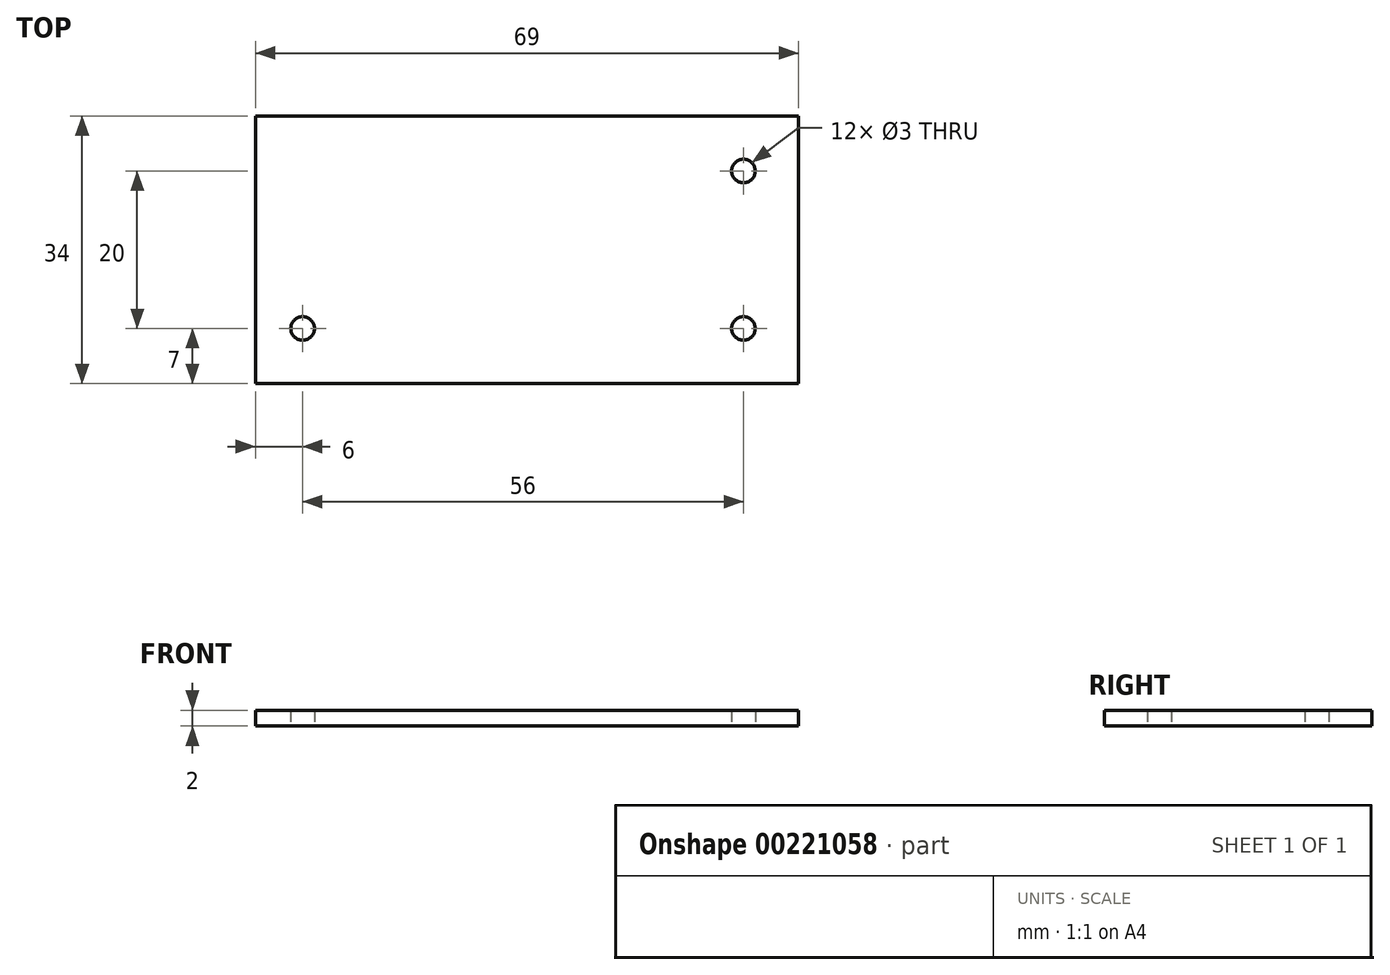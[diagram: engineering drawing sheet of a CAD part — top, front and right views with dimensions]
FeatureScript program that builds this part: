
annotation { "Feature Type Name" : "Feature", "Feature Type Description" : "" }
export const myFeature = defineFeature(function(context is Context, id is Id, definition is map)
    precondition{}
    {
        {
            var Q0;
            Q0=qCreatedBy(makeId("Top.planeOp"),FACE);
            var sketch = newSketch(context, id + "F0", { "sketchPlane" : qUnion([Q0])});
            skLineSegment(sketch, "E0.bottom", {"start": v(-32.5, 15) * mm, "end": v(32.5, 15) * mm});
            skLineSegment(sketch, "E0.top", {"start": v(-32.5, -15) * mm, "end": v(32.5, -15) * mm});
            skLineSegment(sketch, "E0.left", {"start": v(-32.5, 15) * mm, "end": v(-32.5, -15) * mm});
            skLineSegment(sketch, "E0.right", {"start": v(32.5, 15) * mm, "end": v(32.5, -15) * mm});
            skCircle(sketch, "E1", {"center": v(27.5, 10) * mm, "radius": 1.5 * mm});
            skCircle(sketch, "E2", {"center": v(27.5, -10) * mm, "radius": 1.5 * mm});
            skCircle(sketch, "E3", {"center": v(-28.5, -10) * mm, "radius": 1.5 * mm});
            skLineSegment(sketch, "E4", {"start": v(-32.5, 15) * mm, "end": v(-32.5, 17) * mm});
            skLineSegment(sketch, "E5", {"start": v(-32.5, 17) * mm, "end": v(32.5, 17) * mm});
            skLineSegment(sketch, "E6", {"start": v(32.5, 17) * mm, "end": v(32.5, 15) * mm});
            skLineSegment(sketch, "E7", {"start": v(-32.5, 17) * mm, "end": v(-34.5, 17) * mm});
            skLineSegment(sketch, "E8", {"start": v(-34.5, 17) * mm, "end": v(-34.5, -17) * mm});
            skLineSegment(sketch, "E9", {"start": v(-34.5, -17) * mm, "end": v(-32.5, -17) * mm});
            skLineSegment(sketch, "E10", {"start": v(-32.5, -17) * mm, "end": v(-32.5, -15) * mm});
            skLineSegment(sketch, "E11", {"start": v(-32.5, -17) * mm, "end": v(32.5, -17) * mm});
            skLineSegment(sketch, "E12", {"start": v(32.5, -17) * mm, "end": v(32.5, -15) * mm});
            skLineSegment(sketch, "E13", {"start": v(32.5, -17) * mm, "end": v(34.5, -17) * mm});
            skLineSegment(sketch, "E14", {"start": v(34.5, -17) * mm, "end": v(34.5, 17) * mm});
            skLineSegment(sketch, "E15", {"start": v(34.5, 17) * mm, "end": v(32.5, 17) * mm});
            skSolve(sketch);
        }
        {
            var Q0;
            Q0=makeQuery(id+"F0.imprint","IMPRINT",FACE,{"disambiguationData":[TD([[makeQuery(id+"F0.imprint","IMPRINT",EDGE,{"derivedFrom":sQuery(id+"F0.wireOp",EDGE,"E0.bottom")}),-1.0]])]});
            var Q1;
            Q1=makeQuery(id+"F0.imprint","IMPRINT",FACE,{"disambiguationData":[TD([[makeQuery(id+"F0.imprint","IMPRINT",EDGE,{"derivedFrom":sQuery(id+"F0.wireOp",EDGE,"E0.left")}),-1.0]])]});
            var Q2;
            Q2=makeQuery(id+"F0.imprint","IMPRINT",FACE,{"disambiguationData":[TD([[makeQuery(id+"F0.imprint","IMPRINT",EDGE,{"derivedFrom":sQuery(id+"F0.wireOp",EDGE,"E0.bottom")}),1.0]])]});
            var Q3;
            Q3=makeQuery(id+"F0.imprint","IMPRINT",FACE,{"disambiguationData":[TD([[makeQuery(id+"F0.imprint","IMPRINT",EDGE,{"derivedFrom":sQuery(id+"F0.wireOp",EDGE,"E0.top")}),-1.0]])]});
            var Q4;
            Q4=makeQuery(id+"F0.imprint","IMPRINT",FACE,{"disambiguationData":[TD([[makeQuery(id+"F0.imprint","IMPRINT",EDGE,{"derivedFrom":sQuery(id+"F0.wireOp",EDGE,"E0.right")}),1.0]])]});
            extrude(context, id + "F1", {"entities" : qUnion([Q0, Q1, Q2, Q3, Q4]), "depth" : 2 * mm});
        }
    });
